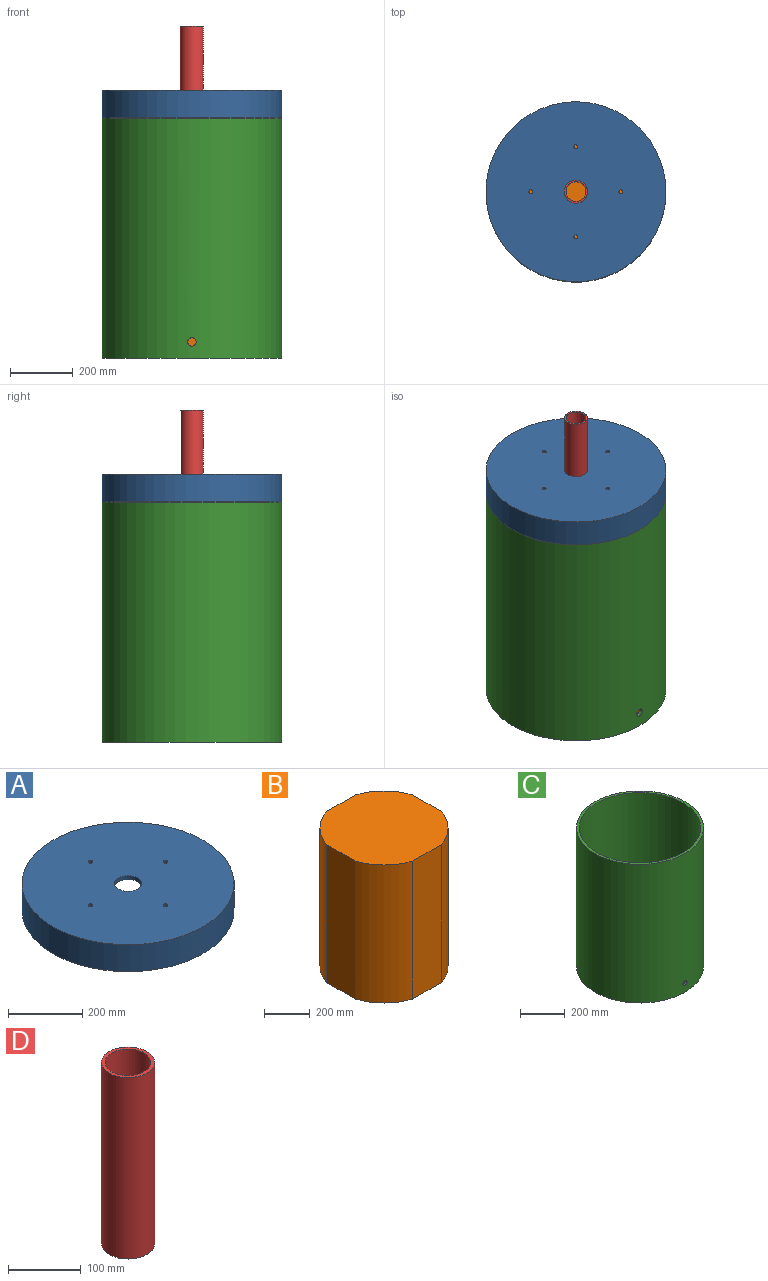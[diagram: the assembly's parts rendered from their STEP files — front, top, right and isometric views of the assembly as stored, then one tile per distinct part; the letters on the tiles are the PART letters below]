
ASSEMBLY  parts=4 mates=3
PART A: 10 faces, bbox 571.5x571.5x88.9 mm
  f0: cylinder r=6.35mm len=12.7mm, axis (0,0,-1), area 506.7mm2, adj f5,f8
  f1: cylinder r=6.35mm len=12.7mm, axis (0,0,-1), area 506.7mm2, adj f5,f8
  f2: cylinder r=6.35mm len=12.7mm, axis (0,0,-1), area 506.7mm2, adj f5,f8
  f3: cylinder r=6.35mm len=12.7mm, axis (0,0,-1), area 506.7mm2, adj f5,f8
  f4: cylinder r=285.75mm len=571.5mm, axis (0,0,-1), area 159612.9mm2, adj f5,f6
  f5: plane 571.5x571.5mm, normal (0,0,1), area 251825.7mm2, adj f0,f1,f2,f3,f4,f9
  f6: plane 571.5x571.5mm, normal (0,0,-1), area 22295.1mm2, adj f4,f7
  f7: cylinder r=273.05mm len=546.1mm, axis (0,0,-1), area 130730.5mm2, adj f6,f8
  f8: plane 546.1x546.1mm, normal (0,0,-1), area 229530.6mm2, adj f0,f1,f2,f3,f7,f9
  f9: cylinder r=36.51mm len=73.03mm, axis (0,0,1), area 2913.6mm2, adj f5,f8
PART B: 10 faces, bbox 529.6x529.6x736.6 mm
  f0: cylinder r=279.4mm len=736.6mm, axis (0,0,-1), area 189620.6mm2, adj f4,f5,f6,f9
  f1: cylinder r=279.4mm len=736.6mm, axis (0,0,-1), area 189620.6mm2, adj f4,f5,f8,f9
  f2: cylinder r=279.4mm len=736.6mm, axis (0,0,-1), area 189620.6mm2, adj f4,f5,f7,f8
  f3: cylinder r=279.4mm len=736.6mm, axis (0,0,-1), area 189620.6mm2, adj f4,f5,f6,f7
  f4: plane 529.6x529.6mm, normal (0,0,1), area 238267.5mm2, adj f0,f1,f2,f3,f6,f7,f8,f9
  f5: plane 529.6x529.6mm, normal (0,0,-1), area 238267.5mm2, adj f0,f1,f2,f3,f6,f7,f8,f9
  f6: plane 736.6x178.28mm, normal (1,0,0), area 131322.2mm2, adj f0,f3,f4,f5
  f7: plane 736.6x178.28mm, normal (0,-1,0), area 131322.2mm2, adj f2,f3,f4,f5
  f8: plane 736.6x178.28mm, normal (-1,0,0), area 131322.2mm2, adj f1,f2,f4,f5
  f9: plane 736.6x178.28mm, normal (0,1,0), area 131322.2mm2, adj f0,f1,f4,f5
PART C: 6 faces, bbox 571.5x571.5x762 mm
  f0: cylinder r=285.75mm len=762mm, axis (0,0,-1), area 1367549.9mm2, adj f2,f3,f5
  f1: cylinder r=273.05mm len=749.3mm, axis (0,0,-1), area 1284956.6mm2, adj f2,f4,f5
  f2: plane 571.5x571.5mm, normal (0,0,1), area 22295.1mm2, adj f0,f1
  f3: plane 571.5x571.5mm, normal (0,0,-1), area 256520.7mm2, adj f0
  f4: plane 546.1x546.1mm, normal (0,0,1), area 234225.5mm2, adj f1
  f5: cylinder r=13.33mm len=26.67mm, axis (0,1,0), area 1064.7mm2, adj f0,f1
PART D: 4 faces, bbox 73x73x304.8 mm
  f0: cylinder r=31.36mm len=304.8mm, axis (0,0,-1), area 60050.9mm2, adj f2,f3
  f1: cylinder r=36.51mm len=304.8mm, axis (0,0,-1), area 69925.6mm2, adj f2,f3
  f2: plane 73.03x73.03mm, normal (0,0,1), area 1099.4mm2, adj f0,f1
  f3: plane 73.03x73.03mm, normal (0,0,-1), area 1099.4mm2, adj f0,f1
PLACE A t=(8.86,-396.22,704.4)mm
PLACE B rot(axis=(0.71,-0.71,0),180deg) t=(8.86,-396.22,691.7)mm
PLACE C t=(8.86,-396.22,-57.6)mm
PLACE D rot(axis=(0,0,-1),90deg) t=(8.86,-396.22,691.7)mm
MATE fastened D.f0 <-> B.f0  axis (0,0,-1) through (8.86,-396.22,691.7)mm
MATE fastened A.f4 <-> C.f0  axis (0,0,-1) through (8.86,-396.22,704.4)mm
MATE fastened B.f0 <-> C.f0  axis (0,0,-1) through (8.86,-396.22,-44.9)mm
